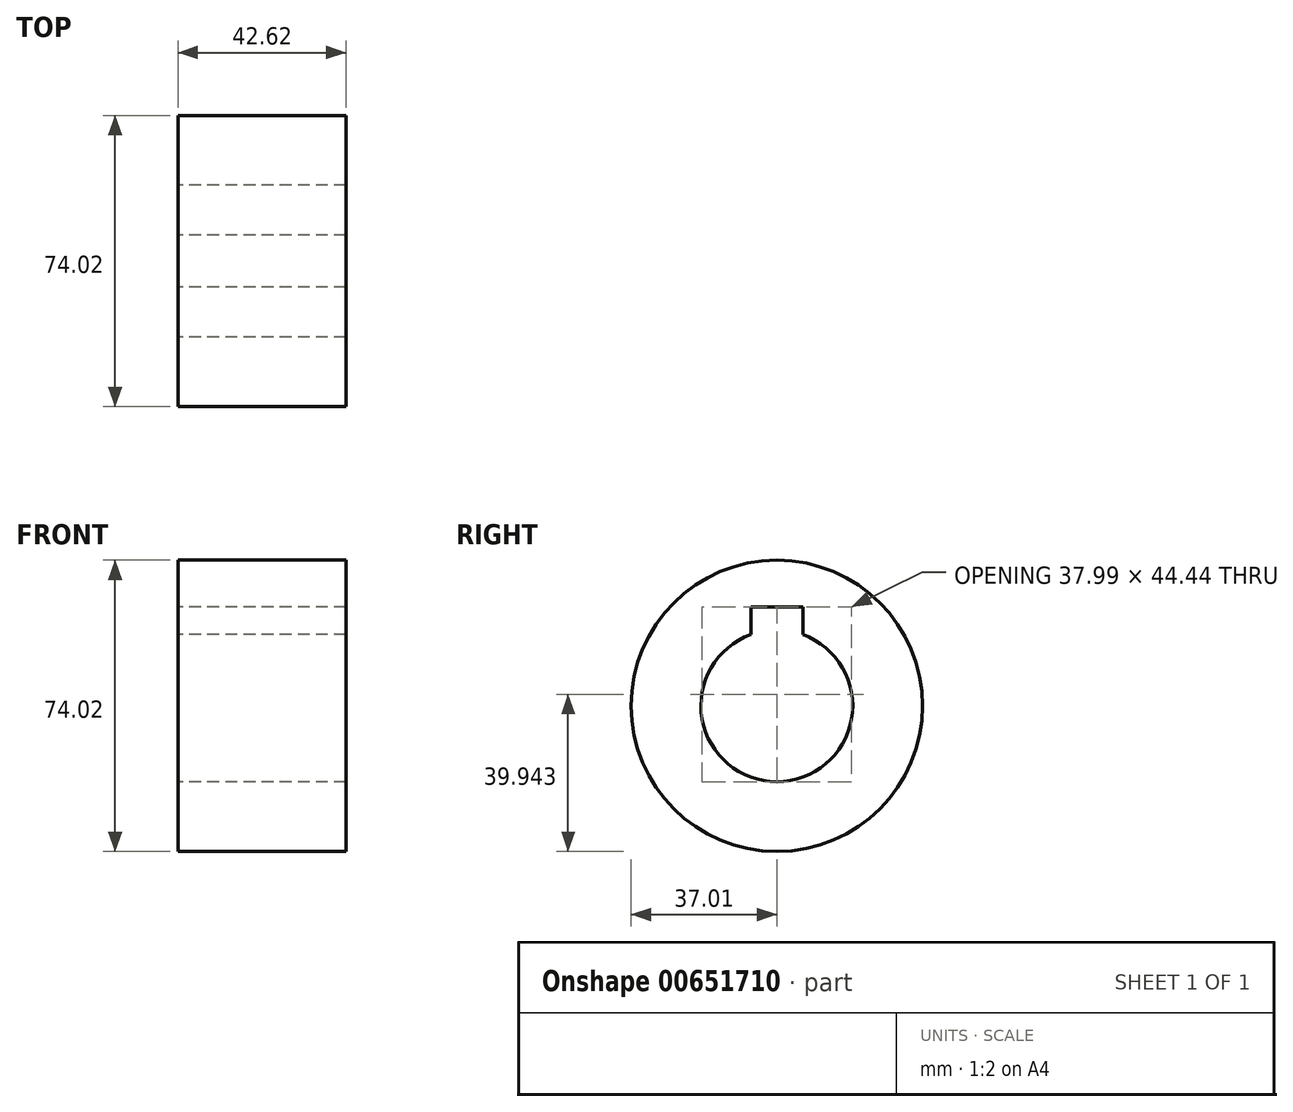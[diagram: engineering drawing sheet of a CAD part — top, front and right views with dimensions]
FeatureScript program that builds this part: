
annotation { "Feature Type Name" : "Feature", "Feature Type Description" : "" }
export const myFeature = defineFeature(function(context is Context, id is Id, definition is map)
    precondition{}
    {
        {
            var Q0;
            Q0=qCreatedBy(makeId("Front.planeOp"),FACE);
            var sketch = newSketch(context, id + "F0", { "sketchPlane" : qUnion([Q0])});
            skLineSegment(sketch, "E0", {"start": v(-76.88, 0) * mm, "end": v(95, 0) * mm, "construction": true});
            skLineSegment(sketch, "E1", {"start": v(0, 19.29) * mm, "end": v(42.62, 19.29) * mm});
            skLineSegment(sketch, "E2", {"start": v(42.62, 19.29) * mm, "end": v(42.62, 37) * mm});
            skLineSegment(sketch, "E3", {"start": v(42.62, 37) * mm, "end": v(0, 37) * mm});
            skLineSegment(sketch, "E4", {"start": v(0, 37) * mm, "end": v(0, 19.29) * mm});
            skSolve(sketch);
        }
        {
            var Q0;
            Q0=makeQuery(id+"F0.imprint","IMPRINT",FACE,{"disambiguationData":[TD([[makeQuery(id+"F0.imprint","IMPRINT",EDGE,{"derivedFrom":sQuery(id+"F0.wireOp",EDGE,"E1")}),1.0]])]});
            var Q1;
            Q1=sQuery(id+"F0.wireOp",EDGE,"E0");
            revolve(context, id + "F1", {"entities" : qUnion([Q0]), "axis" : qUnion([Q1]), "revolveType" : RevolveType.FULL});
        }
        {
            var Q0;
            Q0=qCreatedBy(makeId("Right.planeOp"),FACE);
            var sketch = newSketch(context, id + "F2", { "sketchPlane" : qUnion([Q0])});
            skLineSegment(sketch, "E5.bottom", {"start": v(6.57, 5.63) * mm, "end": v(-6.57, 5.63) * mm});
            skLineSegment(sketch, "E5.top", {"start": v(6.57, 25.15) * mm, "end": v(-6.57, 25.15) * mm});
            skLineSegment(sketch, "E5.left", {"start": v(6.57, 5.63) * mm, "end": v(6.57, 25.15) * mm});
            skLineSegment(sketch, "E5.right", {"start": v(-6.57, 5.63) * mm, "end": v(-6.57, 25.15) * mm});
            skPoint(sketch, "E5.middle", {"position": v(0, 15.4) * mm});
            skSolve(sketch);
        }
        {
            var Q0;
            Q0 = qSketchRegion(id + "F2", true);
            extrude(context, id + "F3", {"entities" : qUnion([Q0]), "operationType" : NewBodyOperationType.REMOVE, "depth" : 78.15 * mm, "offsetDistance" : 25.4 * mm});
        }
    });
